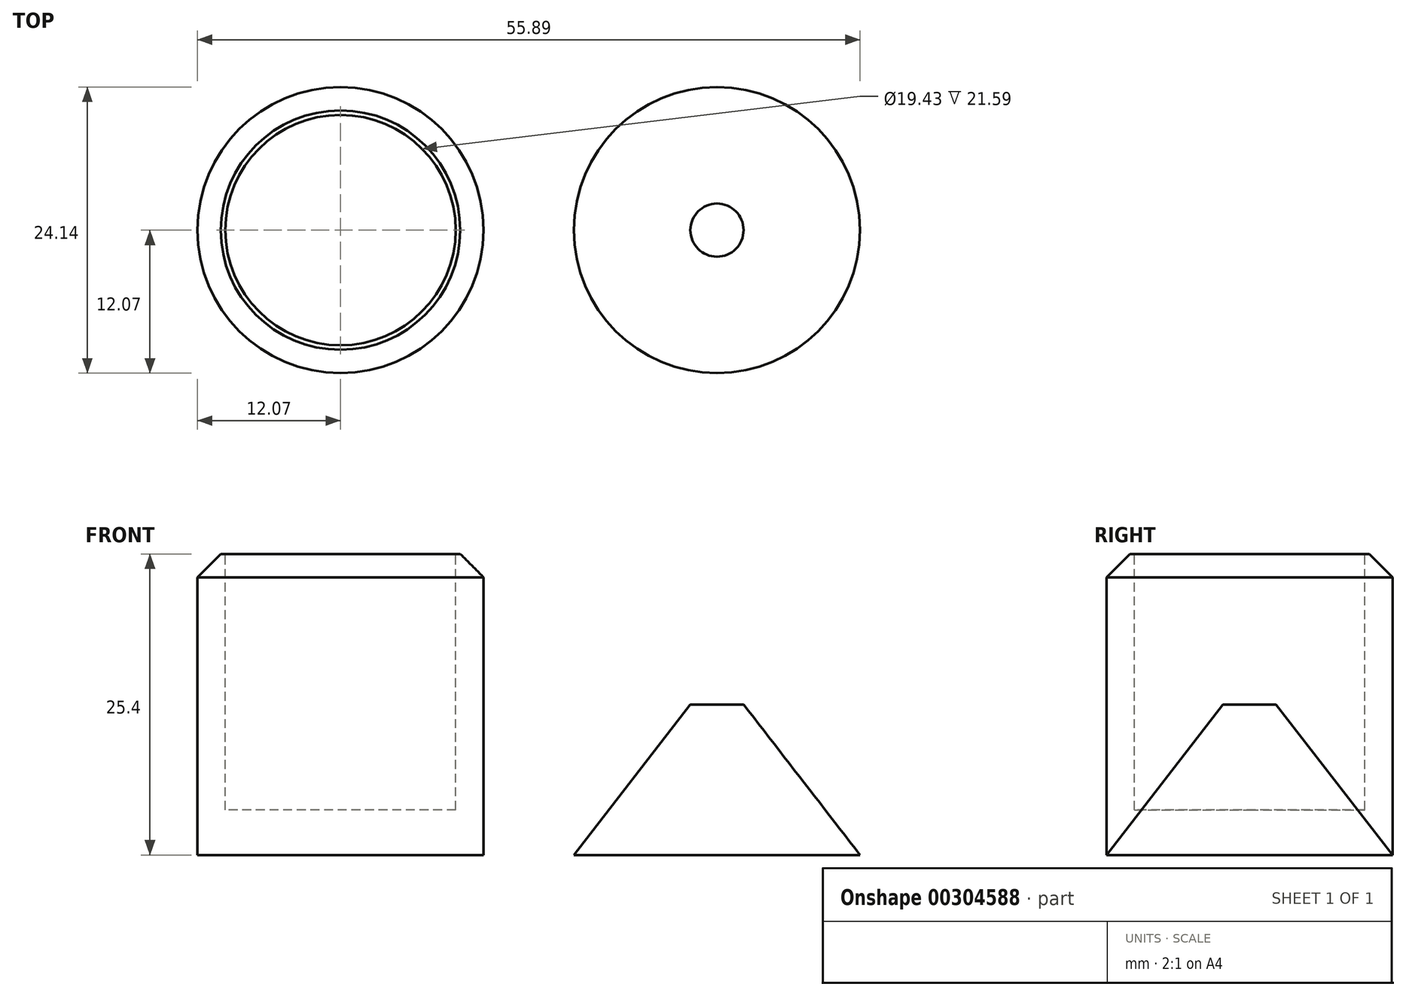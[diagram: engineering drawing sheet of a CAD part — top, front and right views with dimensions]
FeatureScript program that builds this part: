
annotation { "Feature Type Name" : "Feature", "Feature Type Description" : "" }
export const myFeature = defineFeature(function(context is Context, id is Id, definition is map)
    precondition{}
    {
        {
            var Q0;
            Q0=qCreatedBy(makeId("Top.planeOp"),FACE);
            var sketch = newSketch(context, id + "F0", { "sketchPlane" : qUnion([Q0])});
            skCircle(sketch, "E0", {"center": v(0, 0) * mm, "radius": 12.07 * mm});
            skSolve(sketch);
        }
        {
            var Q0;
            Q0 = qSketchRegion(id + "F0", true);
            extrude(context, id + "F1", {"entities" : qUnion([Q0]), "depth" : 25.4 * mm});
        }
        {
            var Q0;
            Q0=makeQuery(id+"F1.opExtrude","CAP_FACE",FACE,{"disambiguationData":[OSD([sQuery(id+"F0.wireOp",EDGE,"E0")])],"isStart":false});
            var sketch = newSketch(context, id + "F2", { "sketchPlane" : qUnion([Q0])});
            skCircle(sketch, "E1", {"center": v(0, 0) * mm, "radius": 9.72 * mm});
            skSolve(sketch);
        }
        {
            var Q0;
            Q0 = qSketchRegion(id + "F2", true);
            extrude(context, id + "F3", {"entities" : qUnion([Q0]), "operationType" : NewBodyOperationType.REMOVE, "oppositeDirection" : true, "depth" : 21.59 * mm});
        }
        {
            var Q0;
            Q0=qCreatedBy(makeId("Top.planeOp"),FACE);
            var sketch = newSketch(context, id + "F4", { "sketchPlane" : qUnion([Q0])});
            skCircle(sketch, "E2", {"center": v(31.75, 0) * mm, "radius": 12.07 * mm});
            skSolve(sketch);
        }
        {
            var Q0;
            Q0=qCreatedBy(makeId("Top.planeOp"),FACE);
            cPlane(context, id + "F5", {"entities" : qUnion([Q0]), "cplaneType" : CPlaneType.OFFSET, "offset" : 12.7 * mm, "width" : 152.4 * mm, "height" : 152.4 * mm});
        }
        {
            var Q0;
            Q0=qCreatedBy(id+"F5.planeOp",FACE);
            var sketch = newSketch(context, id + "F6", { "sketchPlane" : qUnion([Q0])});
            skCircle(sketch, "E3", {"center": v(31.75, 0) * mm, "radius": 2.24 * mm});
            skSolve(sketch);
        }
        {
            var Q0;
            Q0 = qSketchRegion(id + "F4", true);
            var Q1;
            Q1 = qSketchRegion(id + "F6", true);
            loft(context, id + "F7", {"sheetProfilesArray" : [{ "sheetProfileEntities" : qUnion([Q0]) }, { "sheetProfileEntities" : qUnion([Q1]) }]});
        }
        {
            var Q0;
            Q0=makeQuery(id+"F1.opExtrude","CAP_EDGE",EDGE,{"disambiguationData":[OSD([sQuery(id+"F0.wireOp",EDGE,"E0")])],"isStart":false});
            chamfer(context, id + "F8", {"entities" : qUnion([Q0]), "width" : 1.97 * mm, "tangentPropagation" : true});
        }
    });
